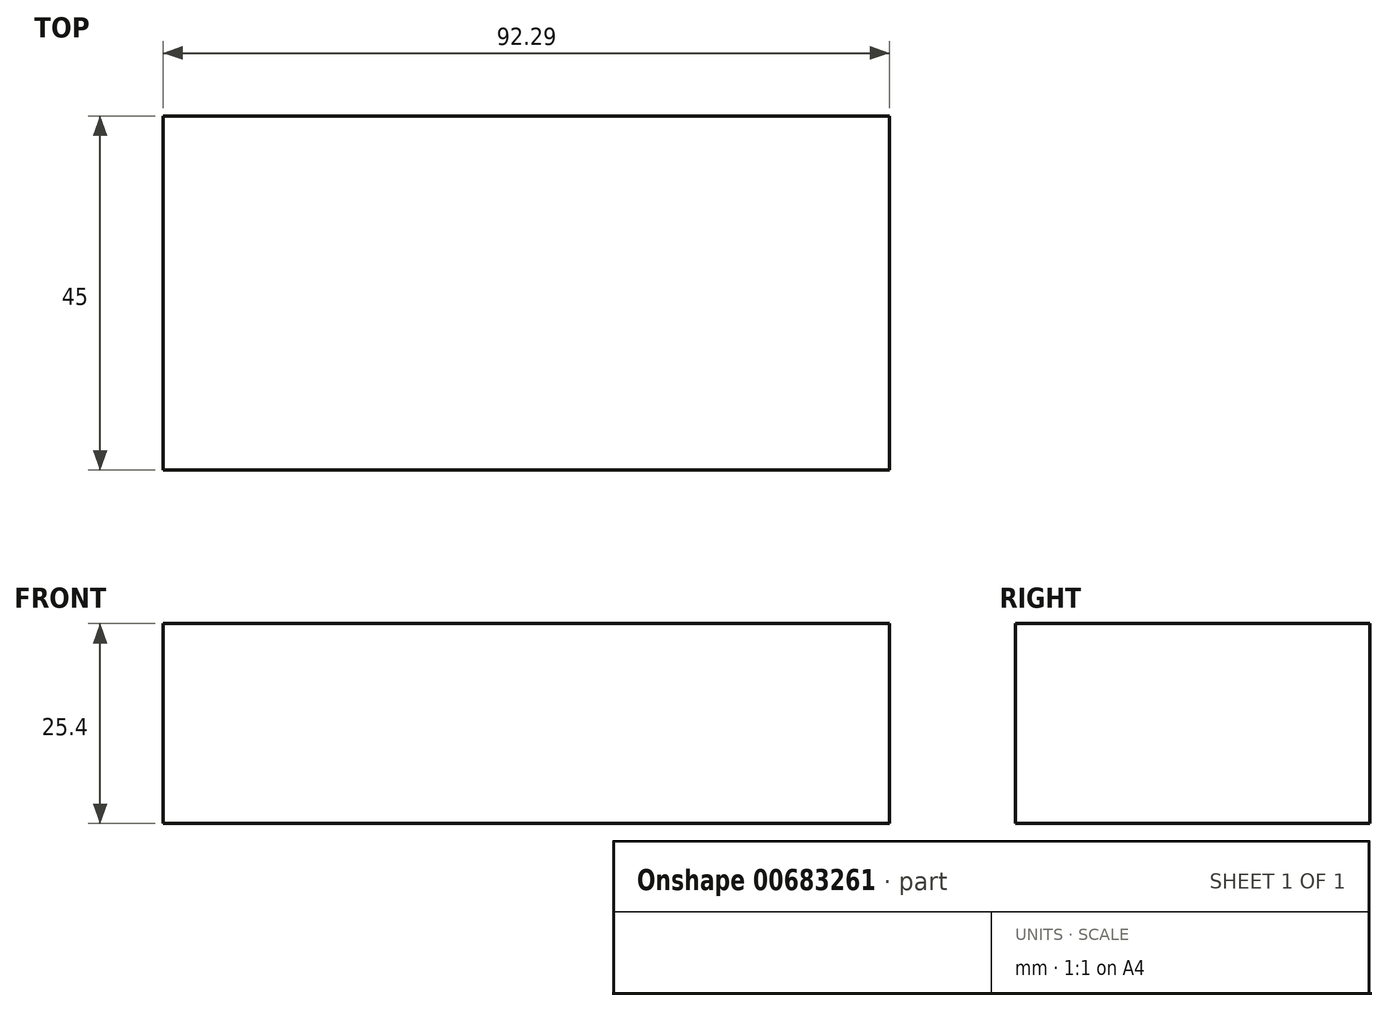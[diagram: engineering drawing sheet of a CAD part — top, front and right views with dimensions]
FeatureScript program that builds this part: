
annotation { "Feature Type Name" : "Feature", "Feature Type Description" : "" }
export const myFeature = defineFeature(function(context is Context, id is Id, definition is map)
    precondition{}
    {
        {
            var Q0;
            Q0=qCreatedBy(makeId("Top.planeOp"),FACE);
            var sketch = newSketch(context, id + "F0", { "sketchPlane" : qUnion([Q0])});
            skLineSegment(sketch, "E0.bottom", {"start": v(-47.17, 22.63) * mm, "end": v(45.12, 22.63) * mm});
            skLineSegment(sketch, "E0.top", {"start": v(-47.17, -22.37) * mm, "end": v(45.12, -22.37) * mm});
            skLineSegment(sketch, "E0.left", {"start": v(-47.17, 22.63) * mm, "end": v(-47.17, -22.37) * mm});
            skLineSegment(sketch, "E0.right", {"start": v(45.12, 22.63) * mm, "end": v(45.12, -22.37) * mm});
            skSolve(sketch);
        }
        {
            var Q0;
            Q0=makeQuery(id+"F0.imprint","IMPRINT",FACE,{"disambiguationData":[TD([[makeQuery(id+"F0.imprint","IMPRINT",EDGE,{"derivedFrom":sQuery(id+"F0.wireOp",EDGE,"E0.bottom")}),-1.0]])]});
            extrude(context, id + "F1", {"entities" : qUnion([Q0]), "depth" : 25.4 * mm, "offsetDistance" : 25.4 * mm});
        }
    });
